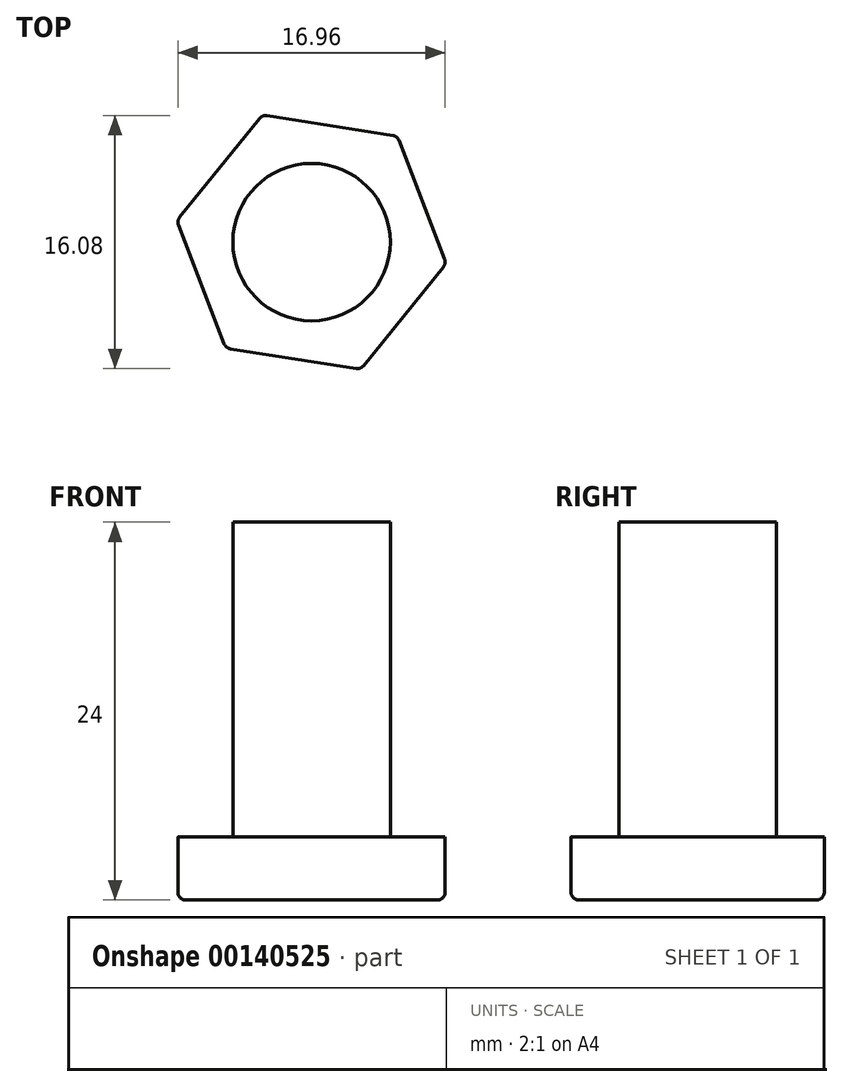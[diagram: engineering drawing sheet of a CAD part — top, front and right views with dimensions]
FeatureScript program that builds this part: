
annotation { "Feature Type Name" : "Feature", "Feature Type Description" : "" }
export const myFeature = defineFeature(function(context is Context, id is Id, definition is map)
    precondition{}
    {
        {
            var Q0;
            Q0=qCreatedBy(makeId("Top.planeOp"),FACE);
            var sketch = newSketch(context, id + "F0", { "sketchPlane" : qUnion([Q0])});
            skCircle(sketch, "E0.cCircle", {"center": v(0, 0) * mm, "radius": 7.5 * mm, "construction": true});
            skLineSegment(sketch, "E0.0", {"start": v(5.45, 6.73) * mm, "end": v(8.55, -1.35) * mm});
            skLineSegment(sketch, "E0.1", {"start": v(8.55, -1.35) * mm, "end": v(3.1, -8.08) * mm});
            skLineSegment(sketch, "E0.2", {"start": v(3.1, -8.08) * mm, "end": v(-5.45, -6.73) * mm});
            skLineSegment(sketch, "E0.3", {"start": v(-5.45, -6.73) * mm, "end": v(-8.55, 1.35) * mm});
            skLineSegment(sketch, "E0.4", {"start": v(-8.55, 1.35) * mm, "end": v(-3.1, 8.08) * mm});
            skLineSegment(sketch, "E0.5", {"start": v(-3.1, 8.08) * mm, "end": v(5.45, 6.73) * mm});
            skPoint(sketch, "E0.0.midPoint", {"position": v(7, 2.7) * mm});
            skSolve(sketch);
        }
        {
            var Q0;
            Q0 = qSketchRegion(id + "F0", true);
            extrude(context, id + "F1", {"entities" : qUnion([Q0]), "depth" : 4 * mm});
        }
        {
            var Q0;
            Q0=makeQuery(id+"F1.opExtrude","CAP_FACE",FACE,{"disambiguationData":[OSD([sQuery(id+"F0.wireOp",EDGE,"E0.0"),sQuery(id+"F0.wireOp",EDGE,"E0.1"),sQuery(id+"F0.wireOp",EDGE,"E0.2"),sQuery(id+"F0.wireOp",EDGE,"E0.3"),sQuery(id+"F0.wireOp",EDGE,"E0.4"),sQuery(id+"F0.wireOp",EDGE,"E0.5")])],"isStart":false});
            var sketch = newSketch(context, id + "F2", { "sketchPlane" : qUnion([Q0])});
            skCircle(sketch, "E1", {"center": v(0, 0) * mm, "radius": 5 * mm});
            skSolve(sketch);
        }
        {
            var Q0;
            Q0 = qSketchRegion(id + "F2", true);
            extrude(context, id + "F3", {"entities" : qUnion([Q0]), "operationType" : NewBodyOperationType.ADD, "depth" : 20 * mm});
        }
        {
            var Q0;
            Q0=makeQuery(id+"F1.opExtrude","CAP_EDGE",EDGE,{"disambiguationData":[OSD([sQuery(id+"F0.wireOp",EDGE,"E0.0")])],"isStart":true});
            var Q1;
            Q1=makeQuery(id+"F1.opExtrude","CAP_EDGE",EDGE,{"disambiguationData":[OSD([sQuery(id+"F0.wireOp",EDGE,"E0.5")])],"isStart":true});
            var Q2;
            Q2=makeQuery(id+"F1.opExtrude","CAP_EDGE",EDGE,{"disambiguationData":[OSD([sQuery(id+"F0.wireOp",EDGE,"E0.4")])],"isStart":true});
            var Q3;
            Q3=makeQuery(id+"F1.opExtrude","CAP_EDGE",EDGE,{"disambiguationData":[OSD([sQuery(id+"F0.wireOp",EDGE,"E0.3")])],"isStart":true});
            var Q4;
            Q4=makeQuery(id+"F1.opExtrude","CAP_EDGE",EDGE,{"disambiguationData":[OSD([sQuery(id+"F0.wireOp",EDGE,"E0.2")])],"isStart":true});
            var Q5;
            Q5=makeQuery(id+"F1.opExtrude","CAP_EDGE",EDGE,{"disambiguationData":[OSD([sQuery(id+"F0.wireOp",EDGE,"E0.1")])],"isStart":true});
            var Q6;
            Q6=makeQuery(id+"F1.opExtrude","SWEPT_EDGE",EDGE,{"disambiguationData":[OSD([sQuery(id+"F0.wireOp",EDGE,"E0.0"),sQuery(id+"F0.wireOp",EDGE,"E0.1")])]});
            var Q7;
            Q7=makeQuery(id+"F1.opExtrude","SWEPT_EDGE",EDGE,{"disambiguationData":[OSD([sQuery(id+"F0.wireOp",EDGE,"E0.0"),sQuery(id+"F0.wireOp",EDGE,"E0.5")])]});
            var Q8;
            Q8=makeQuery(id+"F1.opExtrude","SWEPT_EDGE",EDGE,{"disambiguationData":[OSD([sQuery(id+"F0.wireOp",EDGE,"E0.4"),sQuery(id+"F0.wireOp",EDGE,"E0.5")])]});
            var Q9;
            Q9=makeQuery(id+"F1.opExtrude","SWEPT_EDGE",EDGE,{"disambiguationData":[OSD([sQuery(id+"F0.wireOp",EDGE,"E0.1"),sQuery(id+"F0.wireOp",EDGE,"E0.2")])]});
            var Q10;
            Q10=makeQuery(id+"F1.opExtrude","SWEPT_EDGE",EDGE,{"disambiguationData":[OSD([sQuery(id+"F0.wireOp",EDGE,"E0.3"),sQuery(id+"F0.wireOp",EDGE,"E0.4")])]});
            var Q11;
            Q11=makeQuery(id+"F1.opExtrude","SWEPT_EDGE",EDGE,{"disambiguationData":[OSD([sQuery(id+"F0.wireOp",EDGE,"E0.2"),sQuery(id+"F0.wireOp",EDGE,"E0.3")])]});
            fillet(context, id + "F4", {"entities" : qUnion([Q0, Q1, Q2, Q3, Q4, Q5, Q6, Q7, Q8, Q9, Q10, Q11]), "radius" : 0.5 * mm, "tangentPropagation" : true, "allowEdgeOverflow" : false});
        }
    });
